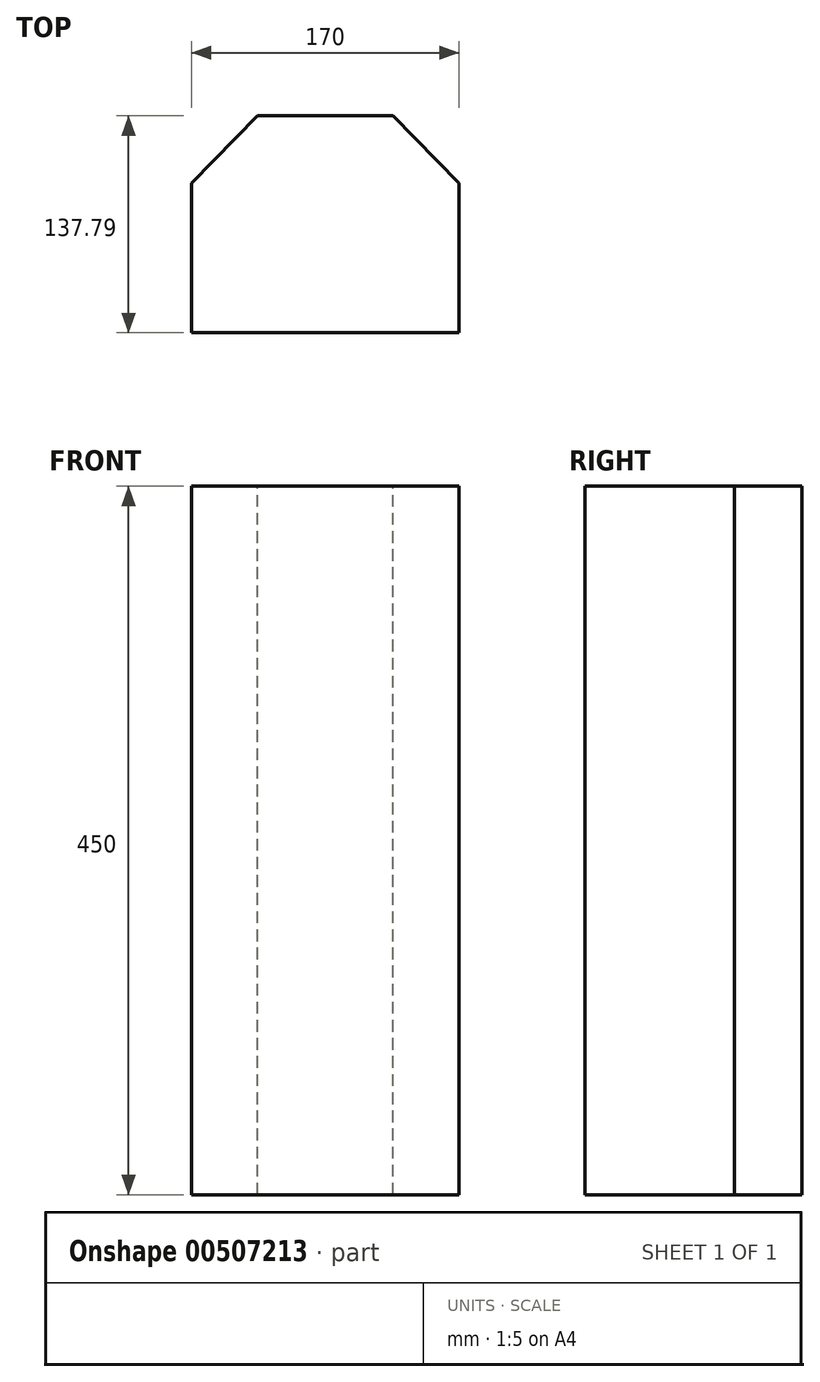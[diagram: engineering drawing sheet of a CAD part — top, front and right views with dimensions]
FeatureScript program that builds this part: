
annotation { "Feature Type Name" : "Feature", "Feature Type Description" : "" }
export const myFeature = defineFeature(function(context is Context, id is Id, definition is map)
    precondition{}
    {
        {
            var Q0;
            Q0=qCreatedBy(makeId("Top.planeOp"),FACE);
            var sketch = newSketch(context, id + "F0", { "sketchPlane" : qUnion([Q0])});
            skLineSegment(sketch, "E0", {"start": v(-120.64, 6.9) * mm, "end": v(49.36, 6.9) * mm});
            skLineSegment(sketch, "E1", {"start": v(49.36, 6.9) * mm, "end": v(49.36, 101.9) * mm});
            skLineSegment(sketch, "E2", {"start": v(49.36, 101.9) * mm, "end": v(7.3, 144.7) * mm});
            skLineSegment(sketch, "E3", {"start": v(7.3, 144.7) * mm, "end": v(-78.58, 144.7) * mm});
            skLineSegment(sketch, "E4", {"start": v(-78.58, 144.7) * mm, "end": v(-120.64, 101.9) * mm});
            skLineSegment(sketch, "E5", {"start": v(-120.64, 6.9) * mm, "end": v(-120.64, 101.9) * mm});
            skSolve(sketch);
        }
        {
            var Q0;
            Q0 = qSketchRegion(id + "F0", true);
            extrude(context, id + "F1", {"entities" : qUnion([Q0]), "oppositeDirection" : true, "depth" : 450 * mm});
        }
    });
